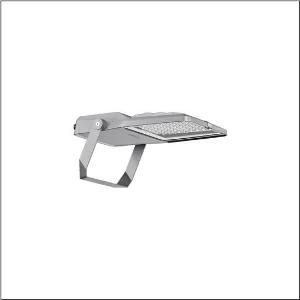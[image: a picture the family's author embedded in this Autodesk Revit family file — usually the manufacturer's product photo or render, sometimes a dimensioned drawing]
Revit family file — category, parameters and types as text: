
# Revit family: floodlight_fl_21_iq_mini___pl61_5xa7772c3c1a_b73e
name_source: partatom
category: Lighting Fixtures
units: mm (PartAtom-declared; Revit-internal decimal feet)

## family parameters
Cut with Voids When Loaded = No
Host = Face
Light Source = No
Part Type = Normal
Room Calculation Point = No
Round Connector Dimension = Use Diameter
Shared = No

## types (1)
- --- (1 x LED, 10320 lm, 87.2 W, 3000K)
    Apparent Load = 87 VA
    CIE Flux Codes = 33 65 98 100 100
    Color Rendering = 80
    Color Temperature = 3000K
    Default Elevation = 1800 mm
    Description = Floodlight FL 21 iQ mini, floodlight, primary light control with lens, of PMMA, primary optical cover: protective disc, of toughened safety glass, transparent, light distribution: PL61, light emission: direct distribution, installation type: surface-mounted, LED, High Power LED, rated luminous flux: 10.320lm, luminous efficacy: 118lm/W, light colour: 830, colour temperature: 3000K, control: Street-Remote, Auto-Match, Temp-Guard, Night-Set, Smart-Wire, Desk-Remote (wireless, voltage-free reading and setting of iQ features in the workshop via application-optimized NFC function/RFID function), optimised constant luminous flux control (CLO 2.0), with terminal, 6-pole, mains connection: 220..240V, AC, 50/60Hz, start of lifetime: 87W, end of service life: 92W, reduction: 40W, luminaire housing, of diecast aluminium, powder-coated, Siteco® metallic grey (DB 702S), corrosivity category C5 mid according to DIN EN ISO 12944, sealing non-destructively replaceable, mounting bracket, of steel, galvanised, powder-coated, Siteco® metallic grey (DB 702S), protection rating (complete): IP66, insulation class (complete): insulation class II (safety insulation), certification: CE, ENEC, VDE, protection symbol: D, impact resistance: IK08, permissible operating ambient temperature: -40..+40°C, permissible operating ambient temperature for outdoor applications: -40..+50°C, standard: DIN EN 12944, LABS conformity tested according to VDMA 24364:2018-05, packaging unit: 1 piece

Light Distribution: PL61
    Height = 70 mm
    Lamp = 1 x LED
    Lamp Light Flux = 10320 lm
    Lamp Power = 87.2 W
    Lamp count = 1
    Length = 485 mm
    Luminous efficacy = 118 lm/W
    Manufacturer = Siteco
    ModVariant = No
    Model = 5XA7772C3C1A
    Number of Poles = 1
    OnlyDefault = Yes
    Power Factor = 1
    Product Name = Floodlight FL 21 iQ mini | PL61
    Product group = floodlight | pylon annexe
    ProductGroupID = 6200
    Protection Class = Protection class II
    Protection Degree = IP 66
    RLX_Detail_Level = 1
    RLX_Emergency_Light_Flux = 0 lm
    RLX_Emergency_Type = 0
    RLX_Emergency_Type_DB = No
    RlxData = <blob elided: 96665 chars, md5=c8b3607e>
    Socket = socket
    Standby Power = 0 W
    System Light Flux = 10320 lm
    System Power = 87 W
    Type Comments = factory setting: luminous flux: 100 % | dim-lin: 254 | 456 mA
    Type Image = l_1006845.jpg
    URL = http://relux.com
    VarID = @adj_123935
    Voltage = 0 V
    Weight = 0.00 kg
    Width = 337 mm

## geometry (parser evidence)
native form markers: Blend x4, Sweep x15
no freeform markers — native parametric forms only
